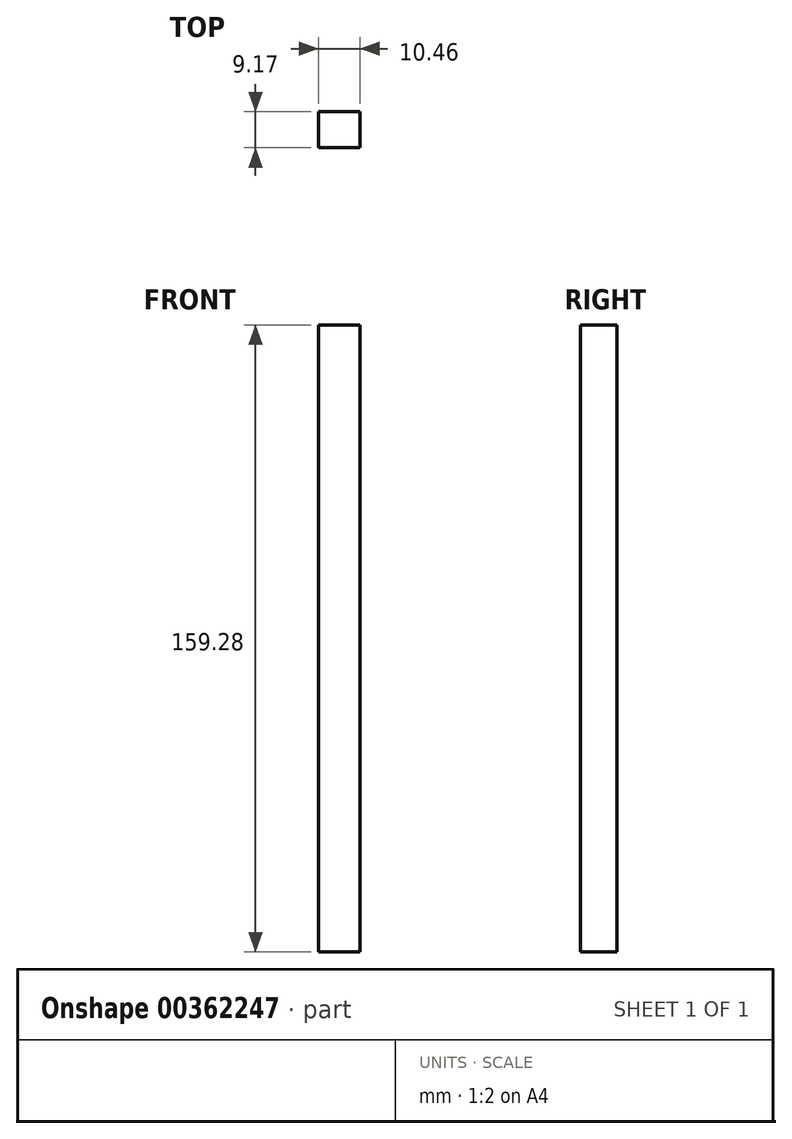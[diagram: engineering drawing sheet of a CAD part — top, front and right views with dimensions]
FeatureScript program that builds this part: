
annotation { "Feature Type Name" : "Feature", "Feature Type Description" : "" }
export const myFeature = defineFeature(function(context is Context, id is Id, definition is map)
    precondition{}
    {
        {
            var Q0;
            Q0=qCreatedBy(makeId("Front.planeOp"),FACE);
            var sketch = newSketch(context, id + "F0", { "sketchPlane" : qUnion([Q0])});
            skLineSegment(sketch, "E0.bottom", {"start": v(5.23, -79.64) * mm, "end": v(-5.23, -79.64) * mm});
            skLineSegment(sketch, "E0.top", {"start": v(5.23, 79.64) * mm, "end": v(-5.23, 79.64) * mm});
            skLineSegment(sketch, "E0.left", {"start": v(5.23, -79.64) * mm, "end": v(5.23, 79.64) * mm});
            skLineSegment(sketch, "E0.right", {"start": v(-5.23, -79.64) * mm, "end": v(-5.23, 79.64) * mm});
            skPoint(sketch, "E0.middle", {"position": v(0, 0) * mm});
            skSolve(sketch);
        }
        {
            var Q0;
            Q0=makeQuery(id+"F0.imprint","IMPRINT",FACE,{"disambiguationData":[TD([[makeQuery(id+"F0.imprint","IMPRINT",EDGE,{"derivedFrom":sQuery(id+"F0.wireOp",EDGE,"E0.bottom")}),-1.0]])]});
            extrude(context, id + "F1", {"entities" : qUnion([Q0]), "depth" : 9.17 * mm});
        }
    });
